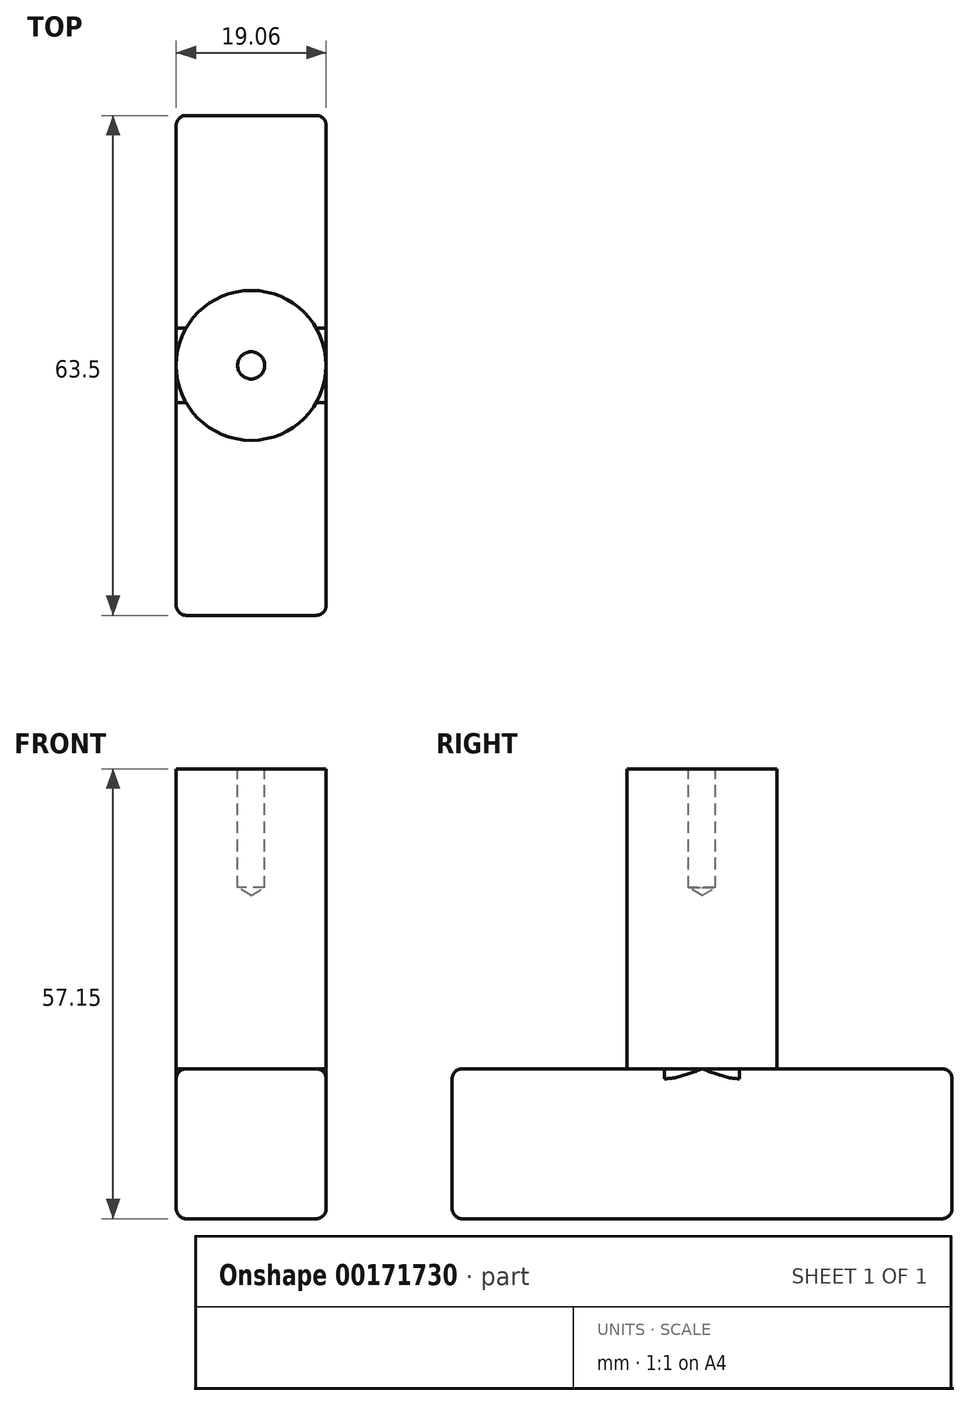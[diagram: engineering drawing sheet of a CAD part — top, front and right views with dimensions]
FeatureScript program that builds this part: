
annotation { "Feature Type Name" : "Feature", "Feature Type Description" : "" }
export const myFeature = defineFeature(function(context is Context, id is Id, definition is map)
    precondition{}
    {
        {
            var Q0;
            Q0=qCreatedBy(makeId("Top.planeOp"),FACE);
            var sketch = newSketch(context, id + "F0", { "sketchPlane" : qUnion([Q0])});
            skCircle(sketch, "E0", {"center": v(0, 0) * mm, "radius": 9.52 * mm});
            skSolve(sketch);
        }
        {
            var Q0;
            Q0=makeQuery(id+"F0.imprint","IMPRINT",FACE,{"disambiguationData":[TD([[makeQuery(id+"F0.imprint","IMPRINT",EDGE,{"derivedFrom":sQuery(id+"F0.wireOp",EDGE,"E0")}),1.0]])]});
            var sketch = newSketch(context, id + "F1", { "sketchPlane" : qUnion([Q0])});
            skLineSegment(sketch, "E1.bottom", {"start": v(9.53, -31.75) * mm, "end": v(-9.53, -31.75) * mm});
            skLineSegment(sketch, "E1.top", {"start": v(9.53, 31.75) * mm, "end": v(-9.52, 31.75) * mm});
            skLineSegment(sketch, "E1.left", {"start": v(9.53, -31.75) * mm, "end": v(9.53, 31.75) * mm});
            skLineSegment(sketch, "E1.right", {"start": v(-9.53, -31.75) * mm, "end": v(-9.52, 31.75) * mm});
            skPoint(sketch, "E1.middle", {"position": v(0, 0) * mm});
            skSolve(sketch);
        }
        {
            var Q0;
            Q0=makeQuery(id+"F0.imprint","IMPRINT",FACE,{"disambiguationData":[TD([[makeQuery(id+"F0.imprint","IMPRINT",EDGE,{"derivedFrom":sQuery(id+"F0.wireOp",EDGE,"E0")}),1.0]])]});
            extrude(context, id + "F2", {"entities" : qUnion([Q0]), "depth" : 38.1 * mm});
        }
        {
            var Q0;
            {var subQ0=sQuery(id+"F1.wireOp",EDGE,"E1.top");Q0=makeQuery(id+"F1.imprint","IMPRINT",FACE,{"disambiguationData":[TD([[makeQuery(id+"F1.imprint","IMPRINT",EDGE,{"derivedFrom":subQ0}),1.0]])]});}
            var Q1;
            {var subQ0=makeQuery(id+"F0.imprint","IMPRINT",EDGE,{"derivedFrom":sQuery(id+"F0.wireOp",EDGE,"E0")});var subQ1=makeQuery(id+"F1.imprint","INTERSECT",VERTEX,{"derivedFrom":[subQ0,sQuery(id+"F1.wireOp",EDGE,"E1.left")]});Q1=makeQuery(id+"F1.imprint","IMPRINT",FACE,{"disambiguationData":[TD([[makeQuery(id+"F1.imprint","IMPRINT",EDGE,{"disambiguationData":[TD([[subQ1,1.0]])],"derivedFrom":subQ0}),1.0]])]});}
            var Q2;
            {var subQ0=sQuery(id+"F1.wireOp",EDGE,"E1.bottom");Q2=makeQuery(id+"F1.imprint","IMPRINT",FACE,{"disambiguationData":[TD([[makeQuery(id+"F1.imprint","IMPRINT",EDGE,{"derivedFrom":subQ0}),-1.0]])]});}
            extrude(context, id + "F3", {"entities" : qUnion([Q0, Q1, Q2]), "operationType" : NewBodyOperationType.ADD, "oppositeDirection" : true, "depth" : 19.05 * mm});
        }
        {
            var Q0;
            Q0=makeQuery(id+"F2.opExtrude","CAP_FACE",FACE,{"disambiguationData":[OSD([sQuery(id+"F0.wireOp",EDGE,"E0")])],"isStart":false});
            var sketch = newSketch(context, id + "F4", { "sketchPlane" : qUnion([Q0])});
            skPoint(sketch, "E2", {"position": v(0, 0) * mm});
            skSolve(sketch);
        }
        {
            var Q0;
            Q0=sQuery(id+"F4.wireOp",VERTEX,"E2");
            var Q1;
            Q1=makeQuery(id+"F2.opExtrude","SWEPT_BODY",BODY,{"disambiguationData":[OSD([sQuery(id+"F0.wireOp",EDGE,"E0")])]});
            hole(context, id + "F5", {"style" : HoleStyle.SIMPLE, "endStyle" : HoleEndStyle.BLIND, "standardTappedOrClearance" : lookupTablePath({ "standard" : "ANSI", "engagement" : "75%", "pitch" : "32 tpi", "size" : "#8", "type" : "Tapped" }), "standardBlindInLast" : lookupTablePath({ "standard" : "ANSI", "engagement" : "75%", "pitch" : "32 tpi", "size" : "#8", "type" : "Tapped" }), "holeDiameter" : 3.45 * mm, "holeDepth" : 15.08 * mm, "startFromSketch" : true, "locations" : qUnion([Q0]), "scope" : qUnion([Q1]), "majorDiameter" : 4.17 * mm, "showTappedDepth" : true, "tappedDepth" : 12.7 * mm, "tapClearance" : 3});
        }
        {
            var Q0;
            {var subQ0=sQuery(id+"F1.wireOp",EDGE,"E1.left");var subQ1=sQuery(id+"F1.wireOp",EDGE,"E1.top");Q0=makeQuery(id+"F3.boolean.opBoolean","SPLIT",EDGE,{"disambiguationData":[TD([makeQuery(id+"F3.opExtrude","SWEPT_FACE",FACE,{"disambiguationData":[OSD([subQ1])]})])],"derivedFrom":makeQuery(id+"F3.opExtrude","CAP_EDGE",EDGE,{"disambiguationData":[OSD([subQ0])],"isStart":true})});}
            var Q1;
            Q1=makeQuery(id+"F3.opExtrude","SWEPT_EDGE",EDGE,{"disambiguationData":[OSD([sQuery(id+"F1.wireOp",EDGE,"E1.bottom"),sQuery(id+"F1.wireOp",EDGE,"E1.left")])]});
            var Q2;
            Q2=makeQuery(id+"F3.opExtrude","CAP_EDGE",EDGE,{"disambiguationData":[OSD([sQuery(id+"F1.wireOp",EDGE,"E1.bottom")])],"isStart":true});
            var Q3;
            Q3=makeQuery(id+"F3.opExtrude","SWEPT_EDGE",EDGE,{"disambiguationData":[OSD([sQuery(id+"F1.wireOp",EDGE,"E1.bottom"),sQuery(id+"F1.wireOp",EDGE,"E1.right")])]});
            var Q4;
            {var subQ0=sQuery(id+"F1.wireOp",EDGE,"E1.bottom");var subQ1=sQuery(id+"F1.wireOp",EDGE,"E1.right");Q4=makeQuery(id+"F3.boolean.opBoolean","SPLIT",EDGE,{"disambiguationData":[TD([makeQuery(id+"F3.opExtrude","SWEPT_FACE",FACE,{"disambiguationData":[OSD([subQ0])]})])],"derivedFrom":makeQuery(id+"F3.opExtrude","CAP_EDGE",EDGE,{"disambiguationData":[OSD([subQ1])],"isStart":true})});}
            var Q5;
            Q5=makeQuery(id+"F3.opExtrude","CAP_EDGE",EDGE,{"disambiguationData":[OSD([sQuery(id+"F1.wireOp",EDGE,"E1.bottom")])],"isStart":false});
            var Q6;
            Q6=makeQuery(id+"F3.opExtrude","CAP_EDGE",EDGE,{"disambiguationData":[OSD([sQuery(id+"F1.wireOp",EDGE,"E1.left")])],"isStart":false});
            var Q7;
            Q7=makeQuery(id+"F3.opExtrude","SWEPT_EDGE",EDGE,{"disambiguationData":[OSD([sQuery(id+"F1.wireOp",EDGE,"E1.top"),sQuery(id+"F1.wireOp",EDGE,"E1.left")])]});
            var Q8;
            Q8=makeQuery(id+"F3.opExtrude","CAP_EDGE",EDGE,{"disambiguationData":[OSD([sQuery(id+"F1.wireOp",EDGE,"E1.top")])],"isStart":true});
            var Q9;
            Q9=makeQuery(id+"F3.opExtrude","CAP_EDGE",EDGE,{"disambiguationData":[OSD([sQuery(id+"F1.wireOp",EDGE,"E1.right")])],"isStart":false});
            var Q10;
            Q10=makeQuery(id+"F3.opExtrude","SWEPT_EDGE",EDGE,{"disambiguationData":[OSD([sQuery(id+"F1.wireOp",EDGE,"E1.top"),sQuery(id+"F1.wireOp",EDGE,"E1.right")])]});
            var Q11;
            Q11=makeQuery(id+"F3.opExtrude","CAP_EDGE",EDGE,{"disambiguationData":[OSD([sQuery(id+"F1.wireOp",EDGE,"E1.top")])],"isStart":false});
            fillet(context, id + "F6", {"entities" : qUnion([Q0, Q1, Q2, Q3, Q4, Q5, Q6, Q7, Q8, Q9, Q10, Q11]), "radius" : 1.27 * mm, "tangentPropagation" : true, "allowEdgeOverflow" : false});
        }
    });
